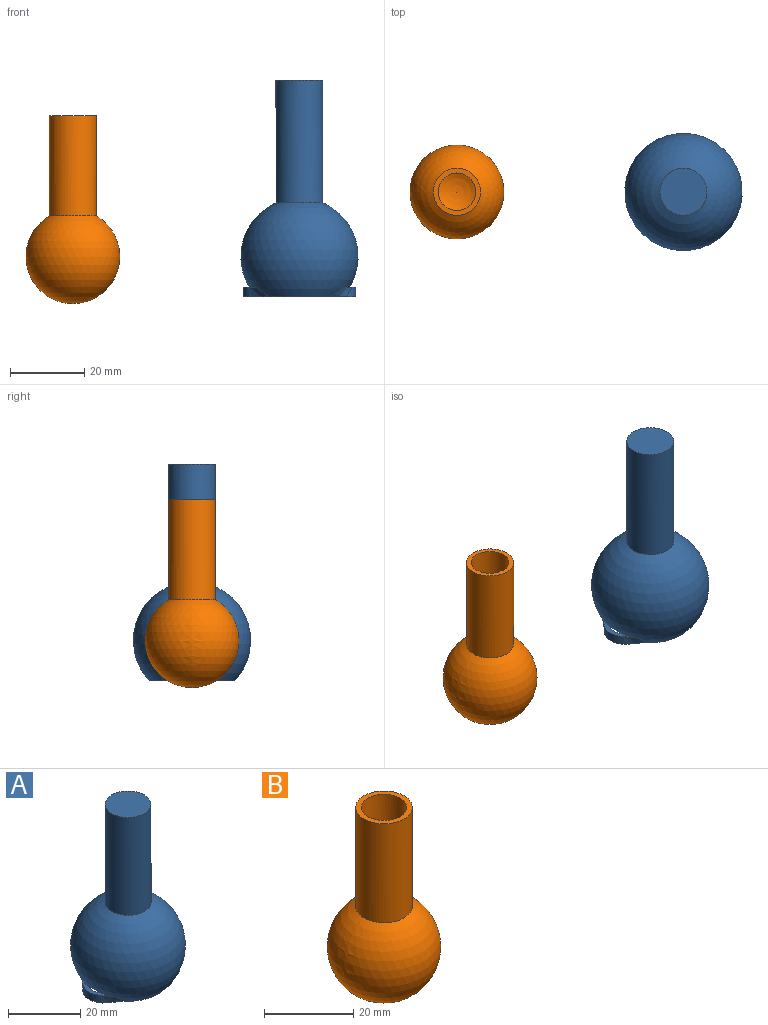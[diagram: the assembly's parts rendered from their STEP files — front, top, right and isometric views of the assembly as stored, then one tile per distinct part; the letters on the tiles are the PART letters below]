
ASSEMBLY  parts=2 mates=1
PART A: 21 faces, bbox 32.3x32.3x63.1 mm
  f0: plane 14.09x3.95mm, normal (0,0,1), area 11.2mm2, adj f1,f2,f8,f17,f18
  f1: cylinder r=4.45mm len=8.82mm, axis (0,0,-1), area 53.4mm2, adj f0,f2,f4,f5,f13,f14
  f2: sphere r=15.88mm, area 2421.4mm2, adj f0,f1,f3,f5,f7,f10,f17,f18
  f3: cylinder r=4.45mm len=8.82mm, axis (0,0,-1), area 53.4mm2, adj f2,f4,f5,f10,f15,f16
  f4: sphere r=14.61mm, area 2135.7mm2, adj f1,f3,f5,f12,f13,f14,f15,f16
  f5: plane 31.01x23.81mm, normal (0,0,-1), area 129.1mm2, adj f1,f2,f3,f4,f8,f9,f13,f14
  f6: plane 12.7x12.7mm, normal (0,0,1), area 126.7mm2, adj f7
  f7: cylinder r=6.35mm len=33.08mm, axis (0,0,-1), area 1319.6mm2, adj f2,f6
  f8: cylinder r=5.71mm len=9.46mm, axis (0,0,-1), area 23.6mm2, adj f0,f5,f17,f18
  f9: cylinder r=5.71mm len=9.46mm, axis (0,0,-1), area 23.6mm2, adj f5,f10,f19,f20
  f10: plane 14.09x3.95mm, normal (0,0,1), area 11.2mm2, adj f2,f3,f9,f19,f20
  f11: plane 10.16x10.16mm, normal (0,0,-1), area 81.1mm2, adj f12
  f12: cylinder r=5.08mm len=32.66mm, axis (0,0,-1), area 1042.5mm2, adj f4,f11
  f13: cylinder r=10.16mm len=1.44mm, axis (0,0,-1), area 0.9mm2, adj f1,f4,f5
  f14: cylinder r=10.16mm len=1.44mm, axis (0,0,-1), area 0.9mm2, adj f1,f4,f5
  f15: cylinder r=10.16mm len=1.44mm, axis (0,0,-1), area 0.9mm2, adj f3,f4,f5
  f16: cylinder r=10.16mm len=1.44mm, axis (0,0,-1), area 0.9mm2, adj f3,f4,f5
  f17: bspline ~9.18x6.8mm, area 13.2mm2, adj f0,f2,f5,f8
  f18: bspline ~9.18x6.8mm, area 13.2mm2, adj f0,f2,f5,f8
  f19: bspline ~9.18x6.8mm, area 13.2mm2, adj f2,f5,f9,f10
  f20: bspline ~9.18x6.8mm, area 13.2mm2, adj f2,f5,f9,f10
PART B: 5 faces, bbox 25.4x25.4x50.8 mm
  f0: sphere r=12.7mm, area 1891.1mm2, adj f2
  f1: plane 12.7x12.7mm, normal (0,0,1), area 45.6mm2, adj f2,f4
  f2: cylinder r=6.35mm len=27.1mm, axis (0,0,-1), area 1081.3mm2, adj f0,f1
  f3: sphere r=11.43mm, area 1556.2mm2, adj f4
  f4: cylinder r=5.08mm len=27.86mm, axis (0,0,-1), area 889.3mm2, adj f1,f3
PLACE A rot(axis=(0,0,-1),180deg) t=(71.61,89.59,-155)mm
PLACE B t=(33.39,63.88,-151.82)mm
MATE pin_slot B.f2 <-> A.f7  axis (0,0,1) through (10.39,89.59,-139.12)mm
